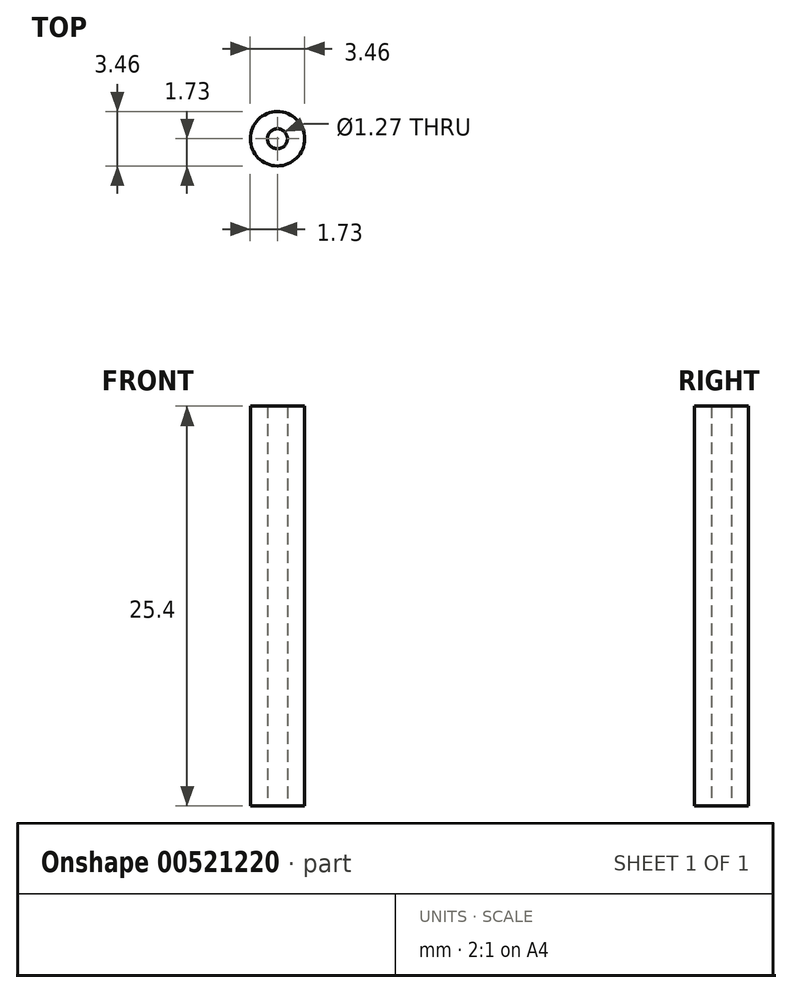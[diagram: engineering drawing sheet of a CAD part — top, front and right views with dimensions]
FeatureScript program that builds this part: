
annotation { "Feature Type Name" : "Feature", "Feature Type Description" : "" }
export const myFeature = defineFeature(function(context is Context, id is Id, definition is map)
    precondition{}
    {
        {
            var Q0;
            Q0=qCreatedBy(makeId("Top.planeOp"),FACE);
            var sketch = newSketch(context, id + "F0", { "sketchPlane" : qUnion([Q0])});
            skCircle(sketch, "E0", {"center": v(0, 0) * mm, "radius": 1.73 * mm});
            skCircle(sketch, "E1", {"center": v(0, 0) * mm, "radius": 0.64 * mm});
            skSolve(sketch);
        }
        {
            var Q0;
            Q0 = qSketchRegion(id + "F0", true);
            extrude(context, id + "F1", {"entities" : qUnion([Q0]), "depth" : 25.4 * mm, "offsetDistance" : 25.4 * mm});
        }
    });
